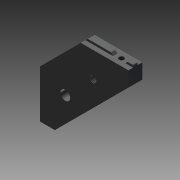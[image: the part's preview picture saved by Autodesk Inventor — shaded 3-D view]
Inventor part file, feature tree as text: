
AUTODESK INVENTOR PART (.ipt)
format: ipt  version: 2016 (Build 200138000, 138)  size: 202,752 bytes
history: native  units: mm
features: other x56, sketch x11, extrude x8, hole x2, revolve x1
ambient origin geometry x8: Origin, YZ Plane, XZ Plane, XY Plane, X Axis, Y Axis, Z Axis, Center Point
bodies: Solid1 (feature_tree)
feature tree (78):
  extrude  "Extrusion1"  Depth=8.0mm TaperAngle=0.0deg
  extrude  "Extrusion2"  Depth=8.0mm TaperAngle=0.0deg
  extrude  "Extrusion3"  TaperAngle=360.0deg  [1 undecoded]
  extrude  "Extrusion4"  Depth=10.0mm TaperAngle=0.0deg
  extrude  "Extrusion5"  [1 undecoded]
  hole  "Drilling 1"  [1 undecoded]
  revolve  "Revolution1"  [1 undecoded]
  extrude  "Extrusion6"  [1 undecoded]
  hole  "Drilling 3"  [1 undecoded]
  extrude  "Extrusion7"  [1 undecoded]
  extrude  "Extrusion8"  [1 undecoded]
  other  "side_2a_XY"
  other  "side_2a_YZ"
  other  "side_2a_ZX"
  other  "side_2a_X"
  other  "side_2a_Y"
  other  "side_2a_Z"
  other  "side_2a_Center"
  other  "side_2b_XY"
  other  "side_2b_YZ"
  other  "side_2b_ZX"
  other  "side_2b_X"
  other  "side_2b_Y"
  other  "side_2b_Z"
  other  "side_2b_Center"
  other  "side_5a_XY"
  other  "side_5a_YZ"
  other  "side_5a_ZX"
  other  "side_5a_X"
  other  "side_5a_Y"
  other  "side_5a_Z"
  other  "side_5a_Center"
  other  "side_5b_XY"
  other  "side_5b_YZ"
  other  "side_5b_ZX"
  other  "side_5b_X"
  other  "side_5b_Y"
  other  "side_5b_Z"
  other  "side_5b_Center"
  other  "side_1a_XY"
  other  "side_1a_YZ"
  other  "side_1a_ZX"
  other  "side_1a_X"
  other  "side_1a_Y"
  other  "side_1a_Z"
  other  "side_1a_Center"
  other  "side_1b_XY"
  other  "side_1b_YZ"
  other  "side_1b_ZX"
  other  "side_1b_X"
  other  "side_1b_Y"
  other  "side_1b_Z"
  other  "side_1b_Center"
  other  "side_6a_XY"
  other  "side_6a_YZ"
  other  "side_6a_ZX"
  other  "side_6a_X"
  other  "side_6a_Y"
  other  "side_6a_Z"
  other  "side_6a_Center"
  other  "side_6b_XY"
  other  "side_6b_YZ"
  other  "side_6b_ZX"
  other  "side_6b_X"
  other  "side_6b_Y"
  other  "side_6b_Z"
  other  "side_6b_Center"
  sketch  "Skizze_1"  dims[d0=25.0mm d1=0.0mm d2=8.0mm d3=0.0mm]
  sketch  "Skizze_2"  dims[d4=8.0mm d5=0.0mm d6=8.0mm d7=0.0mm]
  sketch  "Skizze_3"  dims[d8=8.0mm d9=0.0mm]
  sketch  "Skizze_4"  dims[d10=9.0mm d11=6.0mm d12=4.0mm d13=2.0mm d14=90.0deg d15=92.340434mm d16=0.0mm d17=360.0deg]
  sketch  "Skizze_5"  dims[d18=10.0mm d19=0.0mm]
  sketch  "Sketch6"  dims[d20=11.835mm d21=25.0mm d22=14.0mm d23=2.0mm d24=15.707963mm d25=25.0mm d26=0.0mm d27=10.0mm d28=0.0mm]
  sketch  "Skizze_7"  dims[d29=10.0mm d30=0.0mm]
  sketch  "Skizze_8"
  sketch  "Sketch9"
  sketch  "Skizze_10"
  sketch  "Skizze_11"
note: 8 required parameter values undecoded (feature->parameter linkage not recoverable at this tier; creation-order binding heuristic only, values carry confidence <= 0.55)
